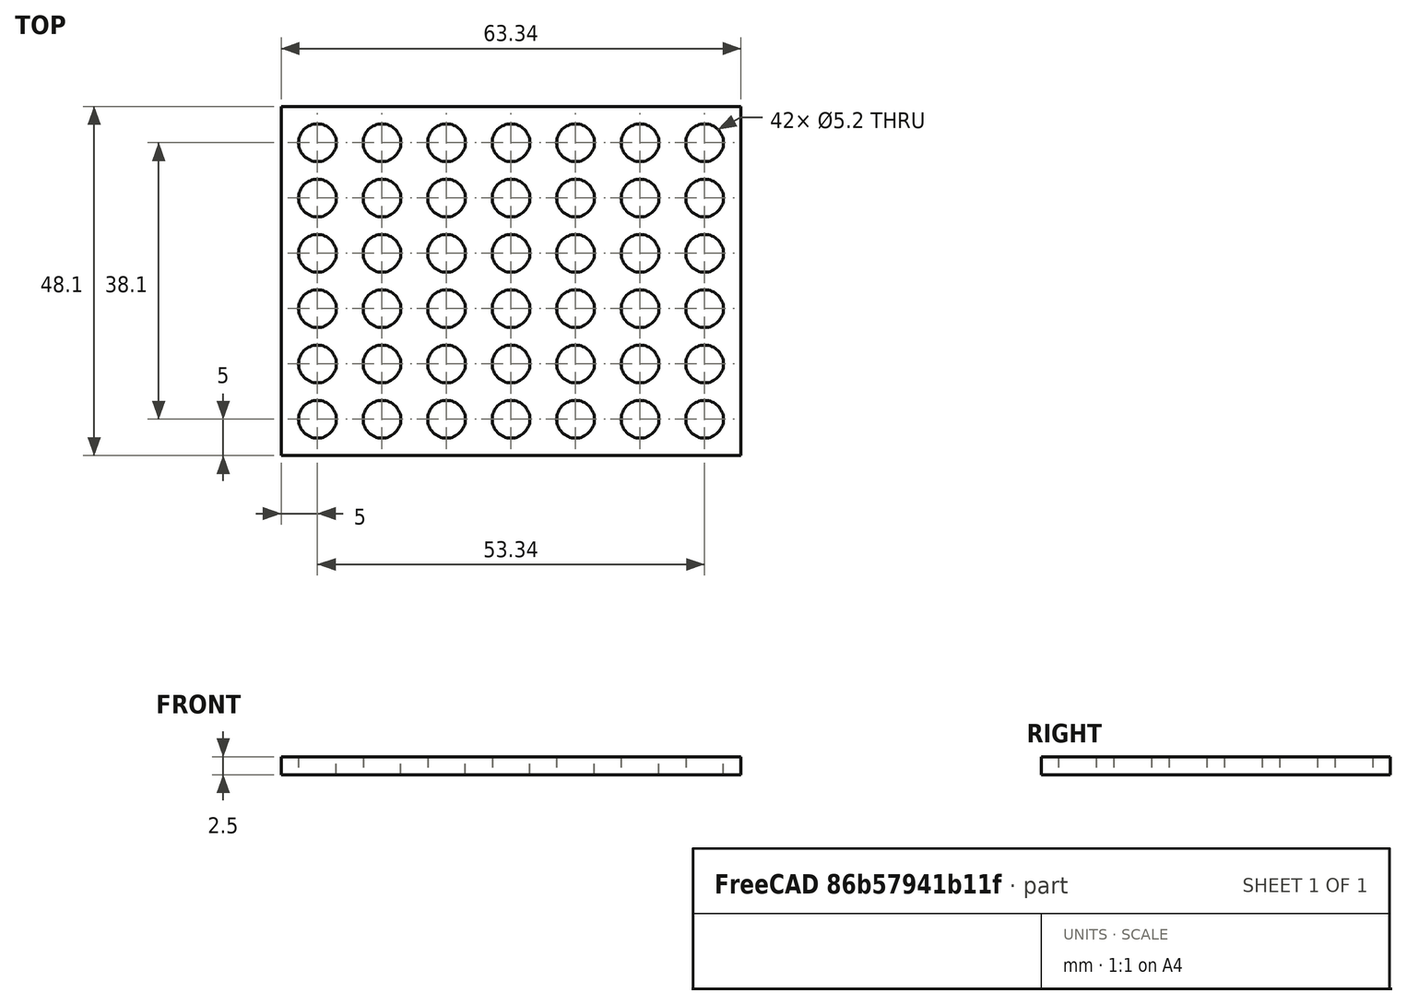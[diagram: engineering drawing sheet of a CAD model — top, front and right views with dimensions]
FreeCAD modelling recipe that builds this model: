
FCSTD DOCUMENT  (FreeCAD 0.18R16117 (Git))
Label: LED Holder
License: All rights reserved
LicenseURL: http://en.wikipedia.org/wiki/All_rights_reserved
objects: Sketcher::SketchObject×1, PartDesign::Pad×1, PartDesign::Body×1
note: 4 computed .brp shape members not serialized (recipe doc carries the construction recipe); baked Part::Feature solids carry a one-line shape summary decoded from their .brp

FEATURE [Sketcher::SketchObject] Sketch
  MapMode = 5
  Support = -> [XY_Plane]
  sketch-geometry (91):
    g0: Circle CenterX=5 CenterY=43.1 CenterZ=0 NormalX=0 NormalY=0 NormalZ=1 AngleXU=0 Radius=2.6
    g1: LineSegment [constr] StartX=5 StartY=43.1 StartZ=0 EndX=13.89 EndY=43.1 EndZ=0
    g2: Circle CenterX=13.89 CenterY=43.1 CenterZ=0 NormalX=0 NormalY=0 NormalZ=1 AngleXU=0 Radius=2.6
    g3: LineSegment [constr] StartX=5 StartY=43.1 StartZ=0 EndX=13.89 EndY=43.1 EndZ=0
    g4: Circle CenterX=22.78 CenterY=43.1 CenterZ=0 NormalX=0 NormalY=0 NormalZ=1 AngleXU=0 Radius=2.6
    g5: LineSegment [constr] StartX=13.89 StartY=43.1 StartZ=0 EndX=22.78 EndY=43.1 EndZ=0
    g6: Circle CenterX=31.67 CenterY=43.1 CenterZ=0 NormalX=0 NormalY=0 NormalZ=1 AngleXU=0 Radius=2.6
    g7: LineSegment [constr] StartX=22.78 StartY=43.1 StartZ=0 EndX=31.67 EndY=43.1 EndZ=0
    g8: Circle CenterX=40.56 CenterY=43.1 CenterZ=0 NormalX=0 NormalY=0 NormalZ=1 AngleXU=0 Radius=2.6
    g9: LineSegment [constr] StartX=31.67 StartY=43.1 StartZ=0 EndX=40.56 EndY=43.1 EndZ=0
    g10: Circle CenterX=49.45 CenterY=43.1 CenterZ=0 NormalX=0 NormalY=0 NormalZ=1 AngleXU=0 Radius=2.6
    g11: LineSegment [constr] StartX=40.56 StartY=43.1 StartZ=0 EndX=49.45 EndY=43.1 EndZ=0
    g12: Circle CenterX=58.34 CenterY=43.1 CenterZ=0 NormalX=0 NormalY=0 NormalZ=1 AngleXU=0 Radius=2.6
    g13: LineSegment [constr] StartX=49.45 StartY=43.1 StartZ=0 EndX=58.34 EndY=43.1 EndZ=0
    g14: Circle CenterX=5 CenterY=35.48 CenterZ=0 NormalX=0 NormalY=0 NormalZ=1 AngleXU=0 Radius=2.6
    g15: LineSegment [constr] StartX=5 StartY=43.1 StartZ=0 EndX=5 EndY=35.48 EndZ=0
    g16: Circle CenterX=13.89 CenterY=35.48 CenterZ=0 NormalX=0 NormalY=0 NormalZ=1 AngleXU=0 Radius=2.6
    g17: LineSegment [constr] StartX=5 StartY=35.48 StartZ=0 EndX=13.89 EndY=35.48 EndZ=0
    g18: Circle CenterX=22.78 CenterY=35.48 CenterZ=0 NormalX=0 NormalY=0 NormalZ=1 AngleXU=0 Radius=2.6
    g19: LineSegment [constr] StartX=13.89 StartY=35.48 StartZ=0 EndX=22.78 EndY=35.48 EndZ=0
    g20: Circle CenterX=31.67 CenterY=35.48 CenterZ=0 NormalX=0 NormalY=0 NormalZ=1 AngleXU=0 Radius=2.6
    g21: LineSegment [constr] StartX=22.78 StartY=35.48 StartZ=0 EndX=31.67 EndY=35.48 EndZ=0
    g22: Circle CenterX=40.56 CenterY=35.48 CenterZ=0 NormalX=0 NormalY=0 NormalZ=1 AngleXU=0 Radius=2.6
    g23: LineSegment [constr] StartX=31.67 StartY=35.48 StartZ=0 EndX=40.56 EndY=35.48 EndZ=0
    g24: Circle CenterX=49.45 CenterY=35.48 CenterZ=0 NormalX=0 NormalY=0 NormalZ=1 AngleXU=0 Radius=2.6
    g25: LineSegment [constr] StartX=40.56 StartY=35.48 StartZ=0 EndX=49.45 EndY=35.48 EndZ=0
    g26: Circle CenterX=58.34 CenterY=35.48 CenterZ=0 NormalX=0 NormalY=0 NormalZ=1 AngleXU=0 Radius=2.6
    g27: LineSegment [constr] StartX=49.45 StartY=35.48 StartZ=0 EndX=58.34 EndY=35.48 EndZ=0
    g28: Circle CenterX=5 CenterY=27.86 CenterZ=0 NormalX=0 NormalY=0 NormalZ=1 AngleXU=0 Radius=2.6
    g29: LineSegment [constr] StartX=5 StartY=35.48 StartZ=0 EndX=5 EndY=27.86 EndZ=0
    g30: Circle CenterX=13.89 CenterY=27.86 CenterZ=0 NormalX=0 NormalY=0 NormalZ=1 AngleXU=0 Radius=2.6
    g31: LineSegment [constr] StartX=5 StartY=27.86 StartZ=0 EndX=13.89 EndY=27.86 EndZ=0
    g32: Circle CenterX=22.78 CenterY=27.86 CenterZ=0 NormalX=0 NormalY=0 NormalZ=1 AngleXU=0 Radius=2.6
    g33: LineSegment [constr] StartX=13.89 StartY=27.86 StartZ=0 EndX=22.78 EndY=27.86 EndZ=0
    g34: Circle CenterX=31.67 CenterY=27.86 CenterZ=0 NormalX=0 NormalY=0 NormalZ=1 AngleXU=0 Radius=2.6
    g35: LineSegment [constr] StartX=22.78 StartY=27.86 StartZ=0 EndX=31.67 EndY=27.86 EndZ=0
    g36: Circle CenterX=40.56 CenterY=27.86 CenterZ=0 NormalX=0 NormalY=0 NormalZ=1 AngleXU=0 Radius=2.6
    g37: LineSegment [constr] StartX=31.67 StartY=27.86 StartZ=0 EndX=40.56 EndY=27.86 EndZ=0
    g38: Circle CenterX=49.45 CenterY=27.86 CenterZ=0 NormalX=0 NormalY=0 NormalZ=1 AngleXU=0 Radius=2.6
    g39: LineSegment [constr] StartX=40.56 StartY=27.86 StartZ=0 EndX=49.45 EndY=27.86 EndZ=0
    g40: Circle CenterX=58.34 CenterY=27.86 CenterZ=0 NormalX=0 NormalY=0 NormalZ=1 AngleXU=0 Radius=2.6
    g41: LineSegment [constr] StartX=49.45 StartY=27.86 StartZ=0 EndX=58.34 EndY=27.86 EndZ=0
    g42: Circle CenterX=5 CenterY=20.24 CenterZ=0 NormalX=0 NormalY=0 NormalZ=1 AngleXU=0 Radius=2.6
    g43: LineSegment [constr] StartX=5 StartY=27.86 StartZ=0 EndX=5 EndY=20.24 EndZ=0
    g44: Circle CenterX=13.89 CenterY=20.24 CenterZ=0 NormalX=0 NormalY=0 NormalZ=1 AngleXU=0 Radius=2.6
    g45: LineSegment [constr] StartX=5 StartY=20.24 StartZ=0 EndX=13.89 EndY=20.24 EndZ=0
    g46: Circle CenterX=22.78 CenterY=20.24 CenterZ=0 NormalX=0 NormalY=0 NormalZ=1 AngleXU=0 Radius=2.6
    g47: LineSegment [constr] StartX=13.89 StartY=20.24 StartZ=0 EndX=22.78 EndY=20.24 EndZ=0
    g48: Circle CenterX=31.67 CenterY=20.24 CenterZ=0 NormalX=0 NormalY=0 NormalZ=1 AngleXU=0 Radius=2.6
    g49: LineSegment [constr] StartX=22.78 StartY=20.24 StartZ=0 EndX=31.67 EndY=20.24 EndZ=0
    g50: Circle CenterX=40.56 CenterY=20.24 CenterZ=0 NormalX=0 NormalY=0 NormalZ=1 AngleXU=0 Radius=2.6
    g51: LineSegment [constr] StartX=31.67 StartY=20.24 StartZ=0 EndX=40.56 EndY=20.24 EndZ=0
    g52: Circle CenterX=49.45 CenterY=20.24 CenterZ=0 NormalX=0 NormalY=0 NormalZ=1 AngleXU=0 Radius=2.6
    g53: LineSegment [constr] StartX=40.56 StartY=20.24 StartZ=0 EndX=49.45 EndY=20.24 EndZ=0
    g54: Circle CenterX=58.34 CenterY=20.24 CenterZ=0 NormalX=0 NormalY=0 NormalZ=1 AngleXU=0 Radius=2.6
    g55: LineSegment [constr] StartX=49.45 StartY=20.24 StartZ=0 EndX=58.34 EndY=20.24 EndZ=0
    g56: Circle CenterX=5 CenterY=12.62 CenterZ=0 NormalX=0 NormalY=0 NormalZ=1 AngleXU=0 Radius=2.6
    g57: LineSegment [constr] StartX=5 StartY=20.24 StartZ=0 EndX=5 EndY=12.62 EndZ=0
    g58: Circle CenterX=13.89 CenterY=12.62 CenterZ=0 NormalX=0 NormalY=0 NormalZ=1 AngleXU=0 Radius=2.6
    g59: LineSegment [constr] StartX=5 StartY=12.62 StartZ=0 EndX=13.89 EndY=12.62 EndZ=0
    g60: Circle CenterX=22.78 CenterY=12.62 CenterZ=0 NormalX=0 NormalY=0 NormalZ=1 AngleXU=0 Radius=2.6
    g61: LineSegment [constr] StartX=13.89 StartY=12.62 StartZ=0 EndX=22.78 EndY=12.62 EndZ=0
    g62: Circle CenterX=31.67 CenterY=12.62 CenterZ=0 NormalX=0 NormalY=0 NormalZ=1 AngleXU=0 Radius=2.6
    g63: LineSegment [constr] StartX=22.78 StartY=12.62 StartZ=0 EndX=31.67 EndY=12.62 EndZ=0
    g64: Circle CenterX=40.56 CenterY=12.62 CenterZ=0 NormalX=0 NormalY=0 NormalZ=1 AngleXU=0 Radius=2.6
    g65: LineSegment [constr] StartX=31.67 StartY=12.62 StartZ=0 EndX=40.56 EndY=12.62 EndZ=0
    g66: Circle CenterX=49.45 CenterY=12.62 CenterZ=0 NormalX=0 NormalY=0 NormalZ=1 AngleXU=0 Radius=2.6
    g67: LineSegment [constr] StartX=40.56 StartY=12.62 StartZ=0 EndX=49.45 EndY=12.62 EndZ=0
    g68: Circle CenterX=58.34 CenterY=12.62 CenterZ=0 NormalX=0 NormalY=0 NormalZ=1 AngleXU=0 Radius=2.6
    g69: LineSegment [constr] StartX=49.45 StartY=12.62 StartZ=0 EndX=58.34 EndY=12.62 EndZ=0
    g70: Circle CenterX=5 CenterY=5 CenterZ=0 NormalX=0 NormalY=0 NormalZ=1 AngleXU=0 Radius=2.6
    g71: LineSegment [constr] StartX=5 StartY=12.62 StartZ=0 EndX=5 EndY=5 EndZ=0
    g72: Circle CenterX=13.89 CenterY=5 CenterZ=0 NormalX=0 NormalY=0 NormalZ=1 AngleXU=0 Radius=2.6
    g73: LineSegment [constr] StartX=5 StartY=5 StartZ=0 EndX=13.89 EndY=5 EndZ=0
    g74: Circle CenterX=22.78 CenterY=5 CenterZ=0 NormalX=0 NormalY=0 NormalZ=1 AngleXU=0 Radius=2.6
    g75: LineSegment [constr] StartX=13.89 StartY=5 StartZ=0 EndX=22.78 EndY=5 EndZ=0
    g76: Circle CenterX=31.67 CenterY=5 CenterZ=0 NormalX=0 NormalY=0 NormalZ=1 AngleXU=0 Radius=2.6
    g77: LineSegment [constr] StartX=22.78 StartY=5 StartZ=0 EndX=31.67 EndY=5 EndZ=0
    g78: Circle CenterX=40.56 CenterY=5 CenterZ=0 NormalX=0 NormalY=0 NormalZ=1 AngleXU=0 Radius=2.6
    g79: LineSegment [constr] StartX=31.67 StartY=5 StartZ=0 EndX=40.56 EndY=5 EndZ=0
    g80: Circle CenterX=49.45 CenterY=5 CenterZ=0 NormalX=0 NormalY=0 NormalZ=1 AngleXU=0 Radius=2.6
    g81: LineSegment [constr] StartX=40.56 StartY=5 StartZ=0 EndX=49.45 EndY=5 EndZ=0
    g82: Circle CenterX=58.34 CenterY=5 CenterZ=0 NormalX=0 NormalY=0 NormalZ=1 AngleXU=0 Radius=2.6
    g83: LineSegment [constr] StartX=49.45 StartY=5 StartZ=0 EndX=58.34 EndY=5 EndZ=0
    g84: LineSegment StartX=0 StartY=0 StartZ=0 EndX=63.34 EndY=0 EndZ=0
    g85: LineSegment StartX=63.34 StartY=0 StartZ=0 EndX=63.34 EndY=48.1 EndZ=0
    g86: LineSegment StartX=63.34 StartY=48.1 StartZ=0 EndX=0 EndY=48.1 EndZ=0
    g87: LineSegment StartX=0 StartY=48.1 StartZ=0 EndX=0 EndY=0 EndZ=0
    g88: LineSegment [constr] StartX=0 StartY=0 StartZ=0 EndX=5 EndY=5 EndZ=0
    g89: LineSegment [constr] StartX=63.34 StartY=48.1 StartZ=0 EndX=58.34 EndY=43.1 EndZ=0
    g90: LineSegment [constr] StartX=5 StartY=43.1 StartZ=0 EndX=0 EndY=48.1 EndZ=0
  constraints (229):
    c: Diameter(g0) = 5.2
    c: Coincident(g1,g0)
    c: Horizontal(g1)
    c: DistanceX(g1,g1) = 8.89
    c: Diameter(g2) = 5.2
    c: Coincident(g0,g3)
    c: Coincident(g2,g3)
    c: Distance(g3) = 8.89
    c: Angle(g3) = 0
    c: Diameter(g4) = 5.2
    c: Coincident(g2,g5)
    c: Coincident(g4,g5)
    c: Equal(g3,g5)
    c: Parallel(g5,g3)
    c: Diameter(g6) = 5.2
    c: Coincident(g4,g7)
    c: Coincident(g6,g7)
    c: Equal(g3,g7)
    c: Parallel(g7,g3)
    c: Diameter(g8) = 5.2
    c: Coincident(g6,g9)
    c: Coincident(g8,g9)
    c: Equal(g3,g9)
    c: Parallel(g9,g3)
    c: Diameter(g10) = 5.2
    c: Coincident(g8,g11)
    c: Coincident(g10,g11)
    c: Equal(g3,g11)
    c: Parallel(g11,g3)
    c: Diameter(g12) = 5.2
    c: Coincident(g10,g13)
    c: Coincident(g12,g13)
    c: Equal(g3,g13)
    c: Parallel(g13,g3)
    c: Diameter(g14) = 5.2
    c: Coincident(g0,g15)
    c: Coincident(g14,g15)
    c: Distance(g15) = 7.62
    c: Perpendicular(g15,g3)
    c: Diameter(g16) = 5.2
    c: Coincident(g14,g17)
    c: Coincident(g16,g17)
    c: Equal(g3,g17)
    c: Parallel(g17,g3)
    c: Diameter(g18) = 5.2
    c: Coincident(g16,g19)
    c: Coincident(g18,g19)
    c: Equal(g3,g19)
    c: Parallel(g19,g3)
    c: Diameter(g20) = 5.2
    c: Coincident(g18,g21)
    c: Coincident(g20,g21)
    c: Equal(g3,g21)
    c: Parallel(g21,g3)
    c: Diameter(g22) = 5.2
    c: Coincident(g20,g23)
    c: Coincident(g22,g23)
    c: Equal(g3,g23)
    c: Parallel(g23,g3)
    c: Diameter(g24) = 5.2
    c: Coincident(g22,g25)
    c: Coincident(g24,g25)
    c: Equal(g3,g25)
    c: Parallel(g25,g3)
    c: Diameter(g26) = 5.2
    c: Coincident(g24,g27)
    c: Coincident(g26,g27)
    c: Equal(g3,g27)
    c: Parallel(g27,g3)
    c: Diameter(g28) = 5.2
    c: Coincident(g14,g29)
    c: Coincident(g28,g29)
    c: Equal(g15,g29)
    c: Perpendicular(g29,g3)
    c: Diameter(g30) = 5.2
    c: Coincident(g28,g31)
    c: Coincident(g30,g31)
    c: Equal(g3,g31)
    c: Parallel(g31,g3)
    c: Diameter(g32) = 5.2
    c: Coincident(g30,g33)
    c: Coincident(g32,g33)
    c: Equal(g3,g33)
    c: Parallel(g33,g3)
    c: Diameter(g34) = 5.2
    c: Coincident(g32,g35)
    c: Coincident(g34,g35)
    c: Equal(g3,g35)
    c: Parallel(g35,g3)
    c: Diameter(g36) = 5.2
    c: Coincident(g34,g37)
    c: Coincident(g36,g37)
    c: Equal(g3,g37)
    c: Parallel(g37,g3)
    c: Diameter(g38) = 5.2
    c: Coincident(g36,g39)
    c: Coincident(g38,g39)
    c: Equal(g3,g39)
    c: Parallel(g39,g3)
    c: Diameter(g40) = 5.2
    c: Coincident(g38,g41)
    c: Coincident(g40,g41)
    c: Equal(g3,g41)
    c: Parallel(g41,g3)
    c: Diameter(g42) = 5.2
    c: Coincident(g28,g43)
    c: Coincident(g42,g43)
    c: Equal(g15,g43)
    c: Perpendicular(g43,g3)
    c: Diameter(g44) = 5.2
    c: Coincident(g42,g45)
    c: Coincident(g44,g45)
    c: Equal(g3,g45)
    c: Parallel(g45,g3)
    c: Diameter(g46) = 5.2
    c: Coincident(g44,g47)
    c: Coincident(g46,g47)
    c: Equal(g3,g47)
    c: Parallel(g47,g3)
    c: Diameter(g48) = 5.2
    c: Coincident(g46,g49)
    c: Coincident(g48,g49)
    c: Equal(g3,g49)
    c: Parallel(g49,g3)
    c: Diameter(g50) = 5.2
    c: Coincident(g48,g51)
    c: Coincident(g50,g51)
    c: Equal(g3,g51)
    c: Parallel(g51,g3)
    c: Diameter(g52) = 5.2
    c: Coincident(g50,g53)
    c: Coincident(g52,g53)
    c: Equal(g3,g53)
    c: Parallel(g53,g3)
    c: Diameter(g54) = 5.2
    c: Coincident(g52,g55)
    c: Coincident(g54,g55)
    c: Equal(g3,g55)
    c: Parallel(g55,g3)
    c: Diameter(g56) = 5.2
    c: Coincident(g42,g57)
    c: Coincident(g56,g57)
    c: Equal(g15,g57)
    c: Perpendicular(g57,g3)
    c: Diameter(g58) = 5.2
    c: Coincident(g56,g59)
    c: Coincident(g58,g59)
    c: Equal(g3,g59)
    c: Parallel(g59,g3)
    c: Diameter(g60) = 5.2
    c: Coincident(g58,g61)
    c: Coincident(g60,g61)
    c: Equal(g3,g61)
    c: Parallel(g61,g3)
    c: Diameter(g62) = 5.2
    c: Coincident(g60,g63)
    c: Coincident(g62,g63)
    c: Equal(g3,g63)
    c: Parallel(g63,g3)
    c: Diameter(g64) = 5.2
    c: Coincident(g62,g65)
    c: Coincident(g64,g65)
    c: Equal(g3,g65)
    c: Parallel(g65,g3)
    c: Diameter(g66) = 5.2
    c: Coincident(g64,g67)
    c: Coincident(g66,g67)
    c: Equal(g3,g67)
    c: Parallel(g67,g3)
    c: Diameter(g68) = 5.2
    c: Coincident(g66,g69)
    c: Coincident(g68,g69)
    c: Equal(g3,g69)
    c: Parallel(g69,g3)
    c: Diameter(g70) = 5.2
    c: Coincident(g56,g71)
    c: Coincident(g70,g71)
    c: Equal(g15,g71)
    c: Perpendicular(g71,g3)
    c: Diameter(g72) = 5.2
    c: Coincident(g70,g73)
    c: Coincident(g72,g73)
    c: Equal(g3,g73)
    c: Parallel(g73,g3)
    c: Diameter(g74) = 5.2
    c: Coincident(g72,g75)
    c: Coincident(g74,g75)
    c: Equal(g3,g75)
    c: Parallel(g75,g3)
    c: Diameter(g76) = 5.2
    c: Coincident(g74,g77)
    c: Coincident(g76,g77)
    c: Equal(g3,g77)
    c: Parallel(g77,g3)
    c: Diameter(g78) = 5.2
    c: Coincident(g76,g79)
    c: Coincident(g78,g79)
    c: Equal(g3,g79)
    c: Parallel(g79,g3)
    c: Diameter(g80) = 5.2
    c: Coincident(g78,g81)
    c: Coincident(g80,g81)
    c: Equal(g3,g81)
    c: Parallel(g81,g3)
    c: Diameter(g82) = 5.2
    c: Coincident(g80,g83)
    c: Coincident(g82,g83)
    c: Equal(g3,g83)
    c: Parallel(g83,g3)
    c: Coincident(g1,g1)
    c: Coincident(g84,g85)
    c: Coincident(g85,g86)
    c: Coincident(g86,g87)
    c: Coincident(g87,g84)
    c: Horizontal(g84)
    c: Horizontal(g86)
    c: Vertical(g85)
    c: Vertical(g87)
    c: Coincident(g84,g-1)
    c: Coincident(g88,g84)
    c: Coincident(g88,g70)
    c: Coincident(g89,g85)
    c: Coincident(g89,g12)
    c: Coincident(g90,g0)
    c: Coincident(g90,g86)
    c: Equal(g90,g88)
    c: Equal(g88,g89)
    c: DistanceX(g88,g88) = 5
    c: DistanceY(g88,g88) = 5
FEATURE [PartDesign::Pad] Pad
  Length = 2.5
  Length2 = 100
  Profile = -> Sketch
  Type = 0
FEATURE [PartDesign::Body] Body
  Group = -> [Sketch,Pad]
  Origin = -> Origin
  Tip = -> Pad
